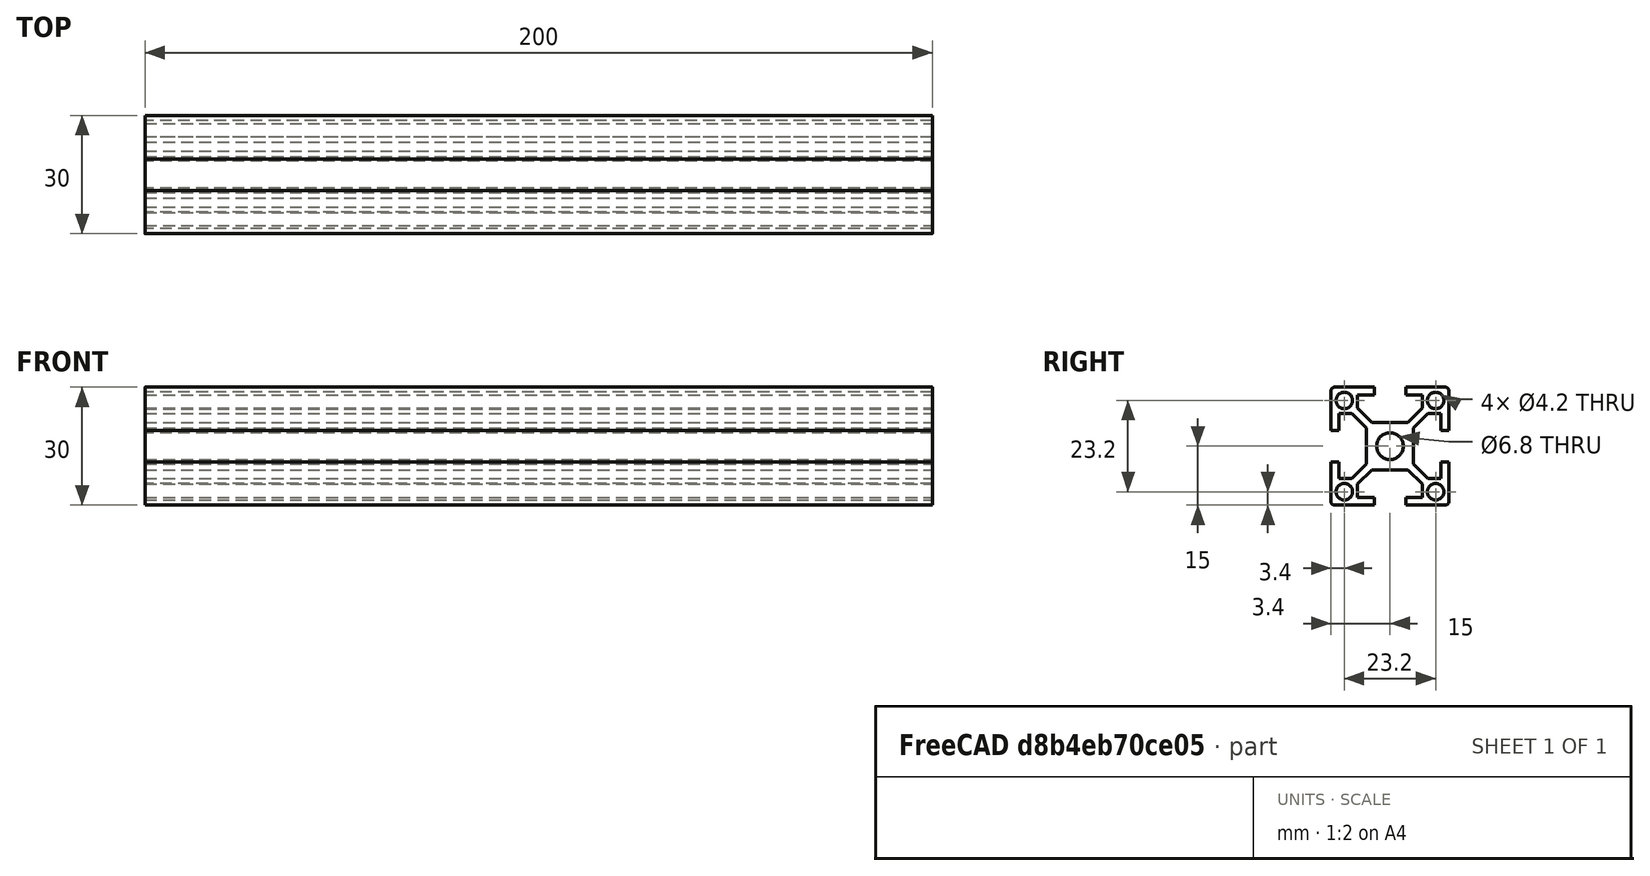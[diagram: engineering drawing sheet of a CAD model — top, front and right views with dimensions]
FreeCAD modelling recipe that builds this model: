
FCSTD DOCUMENT  (FreeCAD 0.15R4671 (Git))
Label: misumi_profile_hfs_serie6_w8_30x30
Comment: Misumi Aluminum profile. HFS serie 6. 30x30mm, width 8
License: CreativeCommons Attribution-ShareAlike
LicenseURL: http://creativecommons.org/licenses/by-sa/4.0/
objects: Sketcher::SketchObject×1, PartDesign::Pad×1
note: 3 computed .brp shape members not serialized (recipe doc carries the construction recipe); baked Part::Feature solids carry a one-line shape summary decoded from their .brp

FEATURE [Sketcher::SketchObject] Sketch  label="perfil"
  Placement = pos=(0,0,0) rot=(0,1,0;1.5708rad)
  sketch-geometry (53):
    g0: LineSegment StartX=-6 StartY=-4.58579 StartZ=0 EndX=-6 EndY=4.58579 EndZ=0
    g1: LineSegment StartX=4.58579 StartY=6 StartZ=0 EndX=-4.58579 EndY=6 EndZ=0
    g2: LineSegment StartX=-6 StartY=4.58579 StartZ=0 EndX=-9.66421 EndY=8.25 EndZ=0
    g3: LineSegment StartX=-4.58579 StartY=6 StartZ=0 EndX=-8.25 EndY=9.66421 EndZ=0
    g4: LineSegment StartX=-9.66421 StartY=8.25 StartZ=0 EndX=-13 EndY=8.25 EndZ=0
    g5: LineSegment StartX=-13 StartY=8.25 StartZ=0 EndX=-13 EndY=4 EndZ=0
    g6: LineSegment StartX=-8.25 StartY=9.66421 StartZ=0 EndX=-8.25 EndY=13 EndZ=0
    g7: LineSegment StartX=-8.25 StartY=13 StartZ=0 EndX=-4 EndY=13 EndZ=0
    g8: LineSegment StartX=-13 StartY=4 StartZ=0 EndX=-15 EndY=4 EndZ=0
    g9: LineSegment StartX=-4 StartY=13 StartZ=0 EndX=-4 EndY=15 EndZ=0
    g10: LineSegment StartX=-4 StartY=15 StartZ=0 EndX=-14 EndY=15 EndZ=0
    g11: LineSegment StartX=-15 StartY=4 StartZ=0 EndX=-15 EndY=14 EndZ=0
    g12: ArcOfCircle CenterX=-14 CenterY=14 CenterZ=0 NormalX=0 NormalY=0 NormalZ=1 Radius=1 StartAngle=1.5708 EndAngle=3.14159
    g13: Circle CenterX=-11.6 CenterY=11.6 CenterZ=0 NormalX=0 NormalY=0 NormalZ=1 Radius=2.1
    g14: Circle CenterX=0 CenterY=0 CenterZ=0 NormalX=0 NormalY=0 NormalZ=1 Radius=3.4
    g15: LineSegment StartX=6 StartY=4.58579 StartZ=0 EndX=6 EndY=-4.58579 EndZ=0
    g16: LineSegment StartX=4.58579 StartY=6 StartZ=0 EndX=8.25 EndY=9.66421 EndZ=0
    g17: LineSegment StartX=8.25 StartY=9.66421 StartZ=0 EndX=8.25 EndY=13 EndZ=0
    g18: LineSegment StartX=8.25 StartY=13 StartZ=0 EndX=4 EndY=13 EndZ=0
    g19: LineSegment StartX=4 StartY=13 StartZ=0 EndX=4 EndY=15 EndZ=0
    g20: LineSegment StartX=6 StartY=4.58579 StartZ=0 EndX=9.66421 EndY=8.25 EndZ=0
    g21: LineSegment StartX=9.66421 StartY=8.25 StartZ=0 EndX=13 EndY=8.25 EndZ=0
    g22: LineSegment StartX=13 StartY=8.25 StartZ=0 EndX=13 EndY=4 EndZ=0
    g23: LineSegment StartX=13 StartY=4 StartZ=0 EndX=15 EndY=4 EndZ=0
    g24: LineSegment StartX=15 StartY=4 StartZ=0 EndX=15 EndY=14 EndZ=0
    g25: Circle CenterX=11.6 CenterY=11.6 CenterZ=0 NormalX=0 NormalY=0 NormalZ=1 Radius=2.1
    g26: LineSegment StartX=4 StartY=15 StartZ=0 EndX=14 EndY=15 EndZ=0
    g27: ArcOfCircle CenterX=14 CenterY=14 CenterZ=0 NormalX=0 NormalY=0 NormalZ=1 Radius=1 StartAngle=6.28319 EndAngle=7.85398
    g28: LineSegment StartX=6 StartY=-4.58579 StartZ=0 EndX=9.66421 EndY=-8.25 EndZ=0
    g29: LineSegment StartX=9.66421 StartY=-8.25 StartZ=0 EndX=13 EndY=-8.25 EndZ=0
    g30: LineSegment StartX=13 StartY=-8.25 StartZ=0 EndX=13 EndY=-4 EndZ=0
    g31: LineSegment StartX=13 StartY=-4 StartZ=0 EndX=15 EndY=-4 EndZ=0
    g32: LineSegment StartX=15 StartY=-4 StartZ=0 EndX=15 EndY=-14 EndZ=0
    g33: LineSegment StartX=14 StartY=-15 StartZ=0 EndX=4 EndY=-15 EndZ=0
    g34: LineSegment StartX=4 StartY=-15 StartZ=0 EndX=4 EndY=-13 EndZ=0
    g35: LineSegment StartX=4 StartY=-13 StartZ=0 EndX=8.25 EndY=-13 EndZ=0
    g36: LineSegment StartX=8.25 StartY=-13 StartZ=0 EndX=8.25 EndY=-9.66421 EndZ=0
    g37: LineSegment StartX=8.25 StartY=-9.66421 StartZ=0 EndX=4.58579 EndY=-6 EndZ=0
    g38: LineSegment StartX=4.58579 StartY=-6 StartZ=0 EndX=-4.58579 EndY=-6 EndZ=0
    g39: LineSegment StartX=-4.58579 StartY=-6 StartZ=0 EndX=-8.25 EndY=-9.66421 EndZ=0
    g40: LineSegment StartX=-8.25 StartY=-9.66421 StartZ=0 EndX=-8.25 EndY=-13 EndZ=0
    g41: LineSegment StartX=-8.25 StartY=-13 StartZ=0 EndX=-4 EndY=-13 EndZ=0
    g42: LineSegment StartX=-4 StartY=-13 StartZ=0 EndX=-4 EndY=-15 EndZ=0
    g43: LineSegment StartX=-4 StartY=-15 StartZ=0 EndX=-14 EndY=-15 EndZ=0
    g44: ArcOfCircle CenterX=14 CenterY=-14 CenterZ=0 NormalX=0 NormalY=0 NormalZ=1 Radius=1 StartAngle=4.71239 EndAngle=6.28319
    g45: LineSegment StartX=-6 StartY=-4.58579 StartZ=0 EndX=-9.66421 EndY=-8.25 EndZ=0
    g46: LineSegment StartX=-9.66421 StartY=-8.25 StartZ=0 EndX=-13 EndY=-8.25 EndZ=0
    g47: LineSegment StartX=-13 StartY=-8.25 StartZ=0 EndX=-13 EndY=-4 EndZ=0
    g48: LineSegment StartX=-13 StartY=-4 StartZ=0 EndX=-15 EndY=-4 EndZ=0
    g49: LineSegment StartX=-15 StartY=-4 StartZ=0 EndX=-15 EndY=-14 EndZ=0
    g50: ArcOfCircle CenterX=-14 CenterY=-14 CenterZ=0 NormalX=0 NormalY=0 NormalZ=1 Radius=0.999995 StartAngle=3.14159 EndAngle=4.71239
    g51: Circle CenterX=-11.6 CenterY=-11.6 CenterZ=0 NormalX=0 NormalY=0 NormalZ=1 Radius=2.1
    g52: Circle CenterX=11.6 CenterY=-11.6 CenterZ=0 NormalX=0 NormalY=0 NormalZ=1 Radius=2.1
  constraints (125):
    c: DistanceX(g-1,g0) = -6
    c: Vertical(g0)
    c: Horizontal(g1)
    c: Equal(g0,g1)
    c: Coincident(g0,g2)
    c: Angle(g2,g0) = 2.35619
    c: Coincident(g3,g1)
    c: Parallel(g2,g3)
    c: Equal(g3,g2)
    c: Coincident(g4,g2)
    c: Horizontal(g4)
    c: Coincident(g4,g5)
    c: Vertical(g5)
    c: Coincident(g6,g3)
    c: Vertical(g6)
    c: Equal(g4,g6)
    c: Coincident(g7,g6)
    c: Horizontal(g7)
    c: Equal(g7,g5)
    c: Coincident(g8,g5)
    c: Horizontal(g8)
    c: Coincident(g9,g7)
    c: Vertical(g9)
    c: DistanceX(g-1,g7) = -4
    c: DistanceY(g9) = 2
    c: Coincident(g10,g9)
    c: Horizontal(g10)
    c: Coincident(g11,g8)
    c: Vertical(g11)
    c: Equal(g10,g11)
    c: DistanceY(g-1,g10) = 15
    c: Coincident(g12,g10)
    c: Coincident(g12,g11)
    c: Radius(g12) = 1
    c: Tangent(g12,g11)
    c: Equal(g8,g9)
    c: Distance(g1,g0) = 2
    c: DistanceX(g-1,g3) = -8.25
    c: Radius(g13) = 2.1
    c: DistanceY(g-1,g13) = 11.6
    c: DistanceX(g-1,g13) = -11.6
    c: Coincident(g14,g-1)
    c: Radius(g14) = 3.4
    c: DistanceY(g-1,g1) = 6
    c: DistanceY(g-1,g5) = 4
    c: Symmetric(g15,g0,g-2)
    c: Symmetric(g0,g15,g-2)
    c: Coincident(g16,g1)
    c: Symmetric(g1,g1,g-2)
    c: Symmetric(g16,g3,g-2)
    c: Coincident(g17,g16)
    c: Symmetric(g17,g6,g-2)
    c: Coincident(g18,g17)
    c: Symmetric(g18,g7,g-2)
    c: Coincident(g19,g18)
    c: Symmetric(g19,g9,g-2)
    c: Coincident(g20,g21)
    c: Coincident(g21,g22)
    c: Coincident(g22,g23)
    c: Coincident(g23,g24)
    c: Coincident(g20,g15)
    c: Symmetric(g20,g2,g-2)
    c: Symmetric(g21,g4,g-2)
    c: Symmetric(g22,g5,g-2)
    c: Symmetric(g23,g8,g-2)
    c: Symmetric(g24,g11,g-2)
    c: Symmetric(g25,g13,g-2)
    c: Equal(g25,g13)
    c: Coincident(g26,g19)
    c: Symmetric(g26,g10,g-2)
    c: Tangent(g27,g26) = 1.5708
    c: Radius(g27) = 1
    c: Coincident(g27,g24)
    c: Coincident(g28,g29)
    c: Coincident(g29,g30)
    c: Coincident(g30,g31)
    c: Coincident(g31,g32)
    c: Coincident(g28,g15)
    c: Symmetric(g28,g20,g-1)
    c: Symmetric(g29,g21,g-1)
    c: Symmetric(g30,g22,g-1)
    c: Symmetric(g31,g23,g-1)
    c: Symmetric(g32,g24,g-1)
    c: Coincident(g33,g34)
    c: Coincident(g34,g35)
    c: Coincident(g35,g36)
    c: Coincident(g36,g37)
    c: Coincident(g37,g38)
    c: Coincident(g38,g39)
    c: Coincident(g39,g40)
    c: Coincident(g40,g41)
    c: Coincident(g41,g42)
    c: Coincident(g42,g43)
    c: Symmetric(g42,g9,g-1)
    c: Symmetric(g41,g7,g-1)
    c: Symmetric(g40,g6,g-1)
    c: Symmetric(g39,g3,g-1)
    c: Symmetric(g38,g1,g-1)
    c: Symmetric(g37,g1,g-1)
    c: Symmetric(g36,g16,g-1)
    c: Symmetric(g35,g17,g-1)
    c: Symmetric(g34,g18,g-1)
    c: Symmetric(g33,g19,g-1)
    c: Symmetric(g33,g26,g-1)
    c: Radius(g44) = 1
    c: Coincident(g44,g33)
    c: Coincident(g44,g32)
    c: Symmetric(g43,g10,g-1)
    c: Coincident(g45,g46)
    c: Coincident(g46,g47)
    c: Coincident(g47,g48)
    c: Coincident(g48,g49)
    c: Coincident(g0,g45)
    c: Symmetric(g45,g2,g-1)
    c: Symmetric(g46,g4,g-1)
    c: Symmetric(g47,g5,g-1)
    c: Symmetric(g48,g8,g-1)
    c: Symmetric(g49,g11,g-1)
    c: Coincident(g50,g49)
    c: Coincident(g50,g43)
    c: Tangent(g50,g49)
    c: Symmetric(g51,g13,g-1)
    c: Equal(g51,g13)
    c: Symmetric(g52,g51,g-2)
    c: Equal(g52,g51)
FEATURE [PartDesign::Pad] Pad  label="perfil_misumi_hfs30x30w8"
  Length = 200
  Length2 = 100
  Placement = pos=(0,0,0) rot=(0,1,0;1.5708rad)
  Sketch = -> Sketch
  Type = 0
